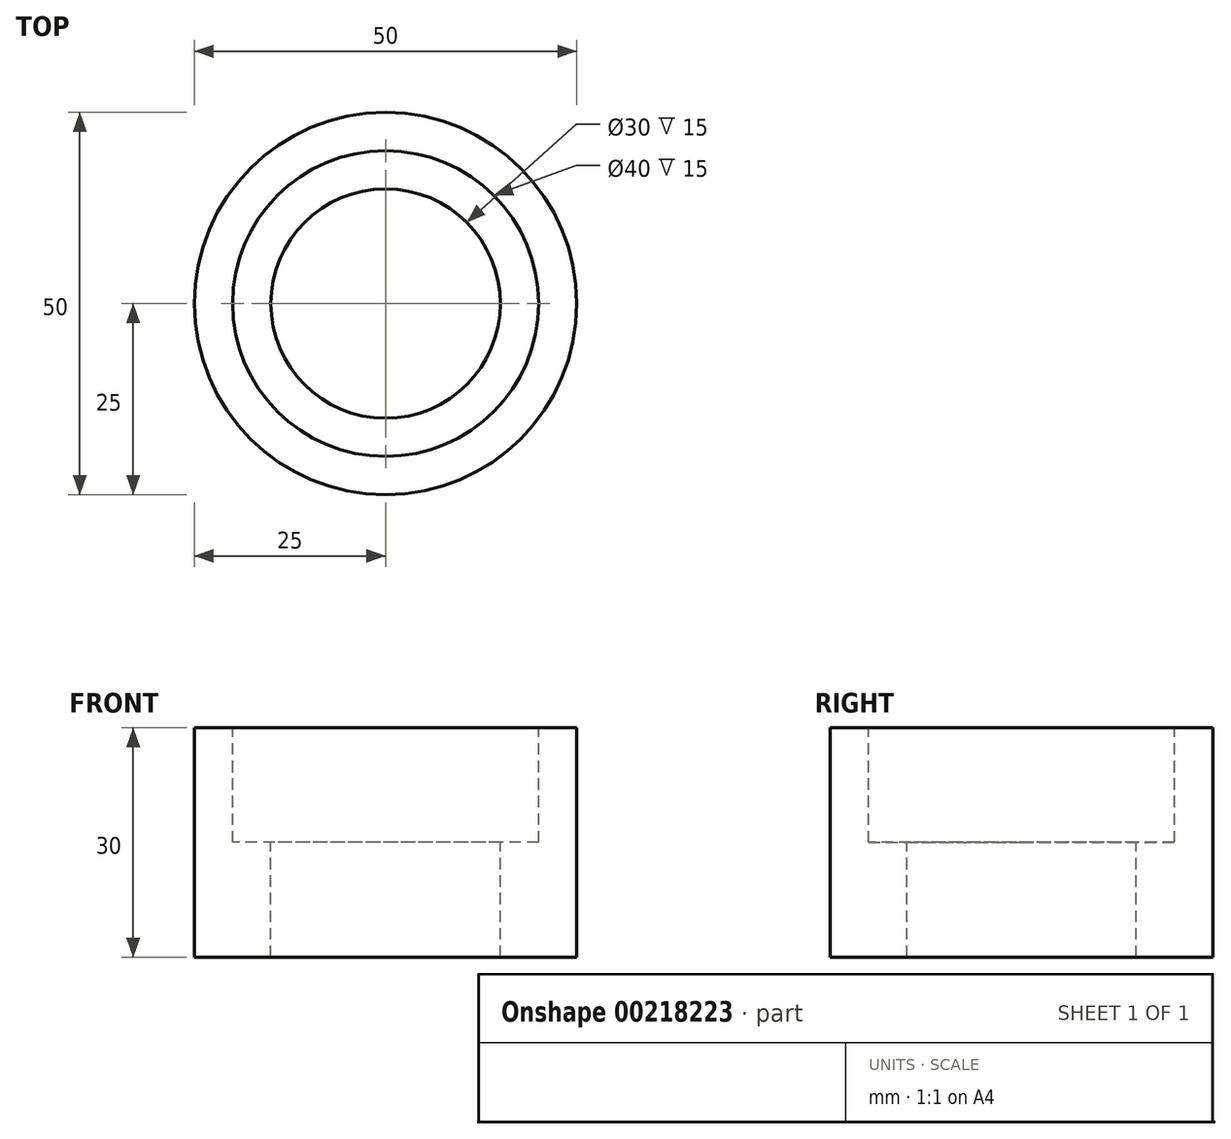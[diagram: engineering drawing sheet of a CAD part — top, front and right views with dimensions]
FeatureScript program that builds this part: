
annotation { "Feature Type Name" : "Feature", "Feature Type Description" : "" }
export const myFeature = defineFeature(function(context is Context, id is Id, definition is map)
    precondition{}
    {
        {
            var Q0;
            Q0=qCreatedBy(makeId("Front.planeOp"),FACE);
            var sketch = newSketch(context, id + "F0", { "sketchPlane" : qUnion([Q0])});
            skLineSegment(sketch, "E0", {"start": v(0, 56.95) * mm, "end": v(0, -65.66) * mm, "construction": true});
            skLineSegment(sketch, "E1.bottom", {"start": v(25, -15) * mm, "end": v(-25, -15) * mm});
            skLineSegment(sketch, "E1.top", {"start": v(25, 15) * mm, "end": v(-25, 15) * mm});
            skLineSegment(sketch, "E1.left", {"start": v(25, -15) * mm, "end": v(25, 15) * mm});
            skLineSegment(sketch, "E1.right", {"start": v(-25, -15) * mm, "end": v(-25, 15) * mm});
            skPoint(sketch, "E1.middle", {"position": v(0, 0) * mm});
            skLineSegment(sketch, "E2", {"start": v(-15, 15) * mm, "end": v(-15, -15) * mm});
            skLineSegment(sketch, "E3.MirrorCS", {"start": v(15, 15) * mm, "end": v(15, -15) * mm});
            skLineSegment(sketch, "E4", {"start": v(-25, 0) * mm, "end": v(-15, 0) * mm});
            skLineSegment(sketch, "E5", {"start": v(-20, 15) * mm, "end": v(-20, 0) * mm});
            skLineSegment(sketch, "E6.MirrorCS", {"start": v(25, 0) * mm, "end": v(15, 0) * mm});
            skLineSegment(sketch, "E7.MirrorCS", {"start": v(20, 15) * mm, "end": v(20, 0) * mm});
            skSolve(sketch);
        }
        {
            var Q0;
            {var subQ1=sQuery(id+"F0.wireOp",EDGE,"E1.bottom");var subQ6=sQuery(id+"F0.wireOp",EDGE,"E1.right");var subQ7=makeQuery(id+"F0.imprint","INTERSECT",VERTEX,{"derivedFrom":[subQ1,subQ6]});Q0=makeQuery(id+"F0.imprint","IMPRINT",FACE,{"disambiguationData":[TD([[makeQuery(id+"F0.imprint","IMPRINT",EDGE,{"disambiguationData":[TD([[subQ7,1.0]])],"derivedFrom":subQ1}),-1.0]])]});}
            var Q1;
            {var subQ3=sQuery(id+"F0.wireOp",EDGE,"E5");Q1=makeQuery(id+"F0.imprint","IMPRINT",FACE,{"disambiguationData":[TD([[makeQuery(id+"F0.imprint","IMPRINT",EDGE,{"derivedFrom":subQ3}),-1.0]])]});}
            var Q2;
            Q2=sQuery(id+"F0.wireOp",EDGE,"E0");
            revolve(context, id + "F1", {"entities" : qUnion([Q0, Q1]), "axis" : qUnion([Q2]), "revolveType" : RevolveType.FULL});
        }
    });
